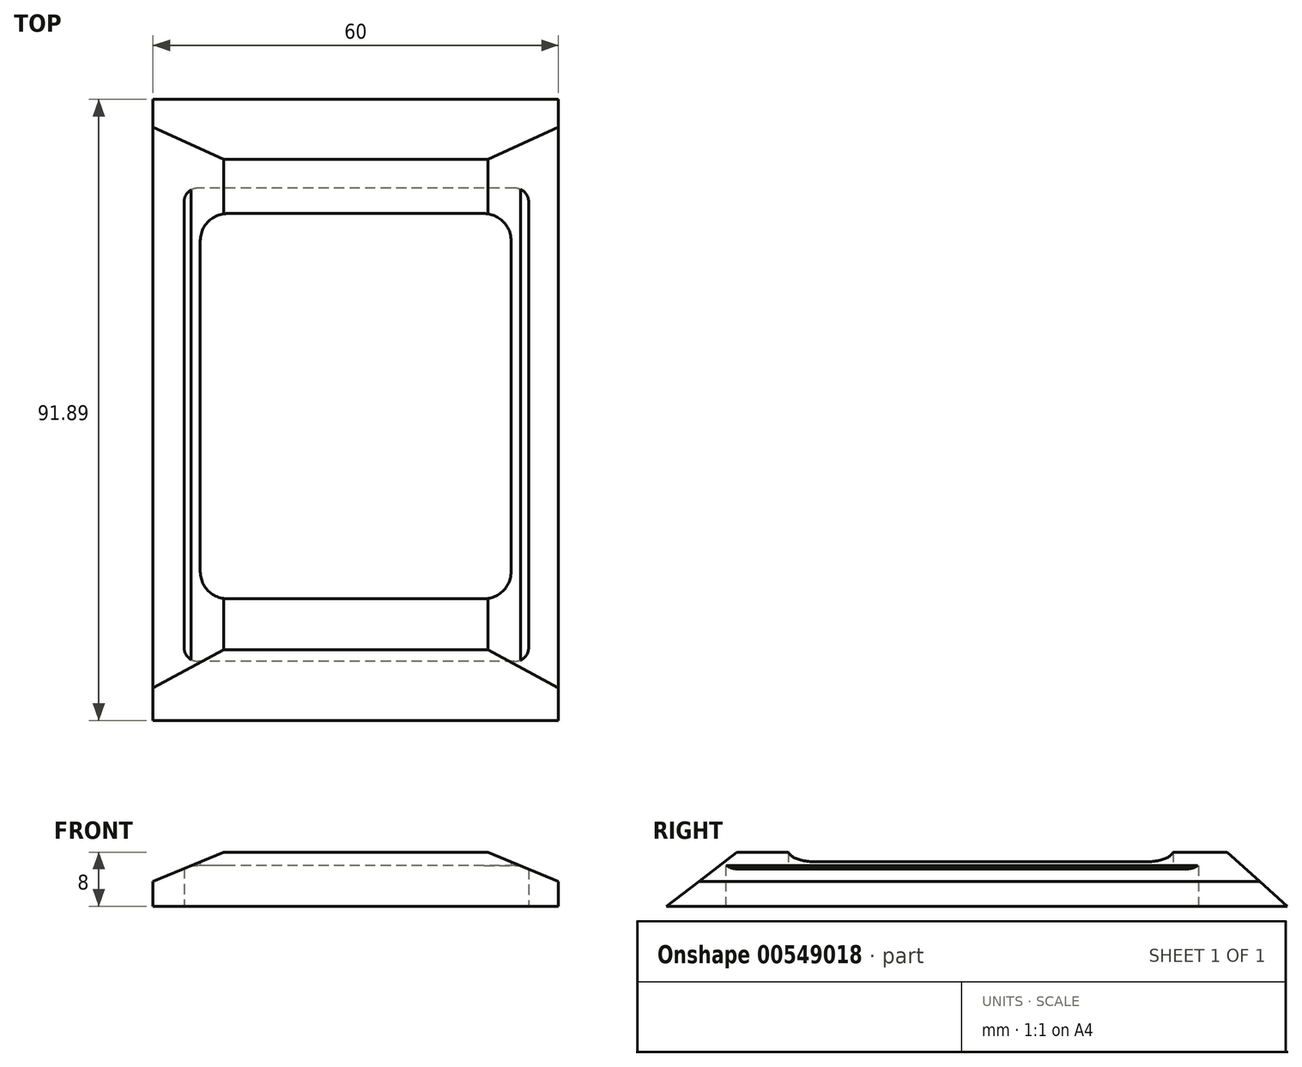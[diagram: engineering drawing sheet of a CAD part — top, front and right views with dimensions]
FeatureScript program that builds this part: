
annotation { "Feature Type Name" : "Feature", "Feature Type Description" : "" }
export const myFeature = defineFeature(function(context is Context, id is Id, definition is map)
    precondition{}
    {
        {
            var Q0;
            Q0=qCreatedBy(makeId("Top.planeOp"),FACE);
            var sketch = newSketch(context, id + "F0", { "sketchPlane" : qUnion([Q0])});
            skPoint(sketch, "E0.middle", {"position": v(0, 0) * mm});
            skLineSegment(sketch, "E1.bottom", {"start": v(19, 28.5) * mm, "end": v(-19, 28.5) * mm});
            skLineSegment(sketch, "E1.top", {"start": v(19, -28.5) * mm, "end": v(-19, -28.5) * mm});
            skLineSegment(sketch, "E1.left", {"start": v(23, 24.5) * mm, "end": v(23, -24.5) * mm});
            skLineSegment(sketch, "E1.right", {"start": v(-23, 24.5) * mm, "end": v(-23, -24.5) * mm});
            skLineSegment(sketch, "E2.bottom", {"start": v(23.6, 32.25) * mm, "end": v(-23.4, 32.25) * mm});
            skLineSegment(sketch, "E2.top", {"start": v(23.6, -37.75) * mm, "end": v(-23.4, -37.75) * mm});
            skLineSegment(sketch, "E2.left", {"start": v(25.6, 30.25) * mm, "end": v(25.6, -35.75) * mm});
            skLineSegment(sketch, "E2.right", {"start": v(-25.4, 30.25) * mm, "end": v(-25.4, -35.75) * mm});
            skPoint(sketch, "E3.visualSharp", {"position": v(25.6, -37.75) * mm});
            skArc(sketch, "E3.filletArc", {"start": v(23.6, -37.75) * mm, "mid": v(25.02, -37.16) * mm, "end": v(25.6, -35.75) * mm});
            skPoint(sketch, "E4.visualSharp", {"position": v(-25.4, -37.75) * mm});
            skArc(sketch, "E4.filletArc", {"start": v(-25.4, -35.75) * mm, "mid": v(-24.81, -37.16) * mm, "end": v(-23.4, -37.75) * mm});
            skPoint(sketch, "E5.visualSharp", {"position": v(-25.4, 32.25) * mm});
            skArc(sketch, "E5.filletArc", {"start": v(-23.4, 32.25) * mm, "mid": v(-24.81, 31.66) * mm, "end": v(-25.4, 30.25) * mm});
            skPoint(sketch, "E6.visualSharp", {"position": v(25.6, 32.25) * mm});
            skArc(sketch, "E6.filletArc", {"start": v(25.6, 30.25) * mm, "mid": v(25.02, 31.66) * mm, "end": v(23.6, 32.25) * mm});
            skPoint(sketch, "E7.visualSharp", {"position": v(23, 28.5) * mm});
            skArc(sketch, "E7.filletArc", {"start": v(23, 24.5) * mm, "mid": v(21.83, 27.33) * mm, "end": v(19, 28.5) * mm});
            skPoint(sketch, "E8.visualSharp", {"position": v(23, -28.5) * mm});
            skArc(sketch, "E8.filletArc", {"start": v(19, -28.5) * mm, "mid": v(21.83, -27.33) * mm, "end": v(23, -24.5) * mm});
            skPoint(sketch, "E9.visualSharp", {"position": v(-23, -28.5) * mm});
            skArc(sketch, "E9.filletArc", {"start": v(-23, -24.5) * mm, "mid": v(-21.83, -27.33) * mm, "end": v(-19, -28.5) * mm});
            skPoint(sketch, "E10.visualSharp", {"position": v(-23, 28.5) * mm});
            skArc(sketch, "E10.filletArc", {"start": v(-19, 28.5) * mm, "mid": v(-21.83, 27.33) * mm, "end": v(-23, 24.5) * mm});
            skSolve(sketch);
        }
        {
            var Q0;
            Q0=qCreatedBy(makeId("Top.planeOp"),FACE);
            var sketch = newSketch(context, id + "F1", { "sketchPlane" : qUnion([Q0])});
            skPoint(sketch, "E11.middle", {"position": v(0, 0) * mm});
            skLineSegment(sketch, "E12.bottom", {"start": v(30, 46.5) * mm, "end": v(-30, 46.5) * mm});
            skLineSegment(sketch, "E12.top", {"start": v(30, -46.5) * mm, "end": v(-30, -46.5) * mm});
            skLineSegment(sketch, "E12.left", {"start": v(30, 46.5) * mm, "end": v(30, -46.5) * mm});
            skLineSegment(sketch, "E12.right", {"start": v(-30, 46.5) * mm, "end": v(-30, -46.5) * mm});
            skSolve(sketch);
        }
        {
            var Q0;
            Q0=makeQuery(id+"F1.imprint","IMPRINT",FACE,{"disambiguationData":[TD([[makeQuery(id+"F1.imprint","IMPRINT",EDGE,{"derivedFrom":sQuery(id+"F1.wireOp",EDGE,"E12.bottom")}),1.0]])]});
            extrude(context, id + "F2", {"entities" : qUnion([Q0]), "depth" : 8 * mm, "offsetDistance" : 25 * mm});
        }
        {
            var Q0;
            Q0=makeQuery(id+"F2.opExtrude","CAP_EDGE",EDGE,{"disambiguationData":[OSD([sQuery(id+"F1.wireOp",EDGE,"E12.left")])],"isStart":false});
            var Q1;
            Q1=makeQuery(id+"F2.opExtrude","CAP_EDGE",EDGE,{"disambiguationData":[OSD([sQuery(id+"F1.wireOp",EDGE,"E12.right")])],"isStart":false});
            chamfer(context, id + "F3", {"entities" : qUnion([Q0, Q1]), "chamferType" : ChamferType.OFFSET_ANGLE, "width" : 4.33 * mm, "oppositeDirection" : true, "angle" : 67.5 * degree});
        }
        {
            var Q0;
            Q0=makeQuery(id+"F2.opExtrude","CAP_EDGE",EDGE,{"disambiguationData":[OSD([sQuery(id+"F1.wireOp",EDGE,"E12.bottom")])],"isStart":false});
            chamfer(context, id + "F4", {"entities" : qUnion([Q0]), "chamferType" : ChamferType.OFFSET_ANGLE, "width" : 9 * mm, "oppositeDirection" : false, "angle" : 48 * degree, "tangentPropagation" : true});
        }
        {
            var Q0;
            Q0=makeQuery(id+"F0.imprint","IMPRINT",FACE,{"disambiguationData":[TD([[makeQuery(id+"F0.imprint","IMPRINT",EDGE,{"derivedFrom":sQuery(id+"F0.wireOp",EDGE,"E1.bottom")}),1.0]])]});
            extrude(context, id + "F5", {"entities" : qUnion([Q0]), "operationType" : NewBodyOperationType.REMOVE, "depth" : 25 * mm, "offsetDistance" : 25 * mm});
        }
        {
            var Q0;
            Q0=makeQuery(id+"F0.imprint","IMPRINT",FACE,{"disambiguationData":[TD([[makeQuery(id+"F0.imprint","IMPRINT",EDGE,{"derivedFrom":sQuery(id+"F0.wireOp",EDGE,"E1.bottom")}),-1.0]])]});
            extrude(context, id + "F6", {"entities" : qUnion([Q0]), "operationType" : NewBodyOperationType.REMOVE, "depth" : 6 * mm, "offsetDistance" : 25 * mm});
        }
        {
            var Q0;
            Q0=makeQuery(id+"F2.opExtrude","CAP_EDGE",EDGE,{"disambiguationData":[OSD([sQuery(id+"F1.wireOp",EDGE,"E12.top")])],"isStart":false});
            chamfer(context, id + "F7", {"entities" : qUnion([Q0]), "chamferType" : ChamferType.OFFSET_ANGLE, "width" : 8 * mm, "oppositeDirection" : true, "angle" : 52.5 * degree});
        }
    });
